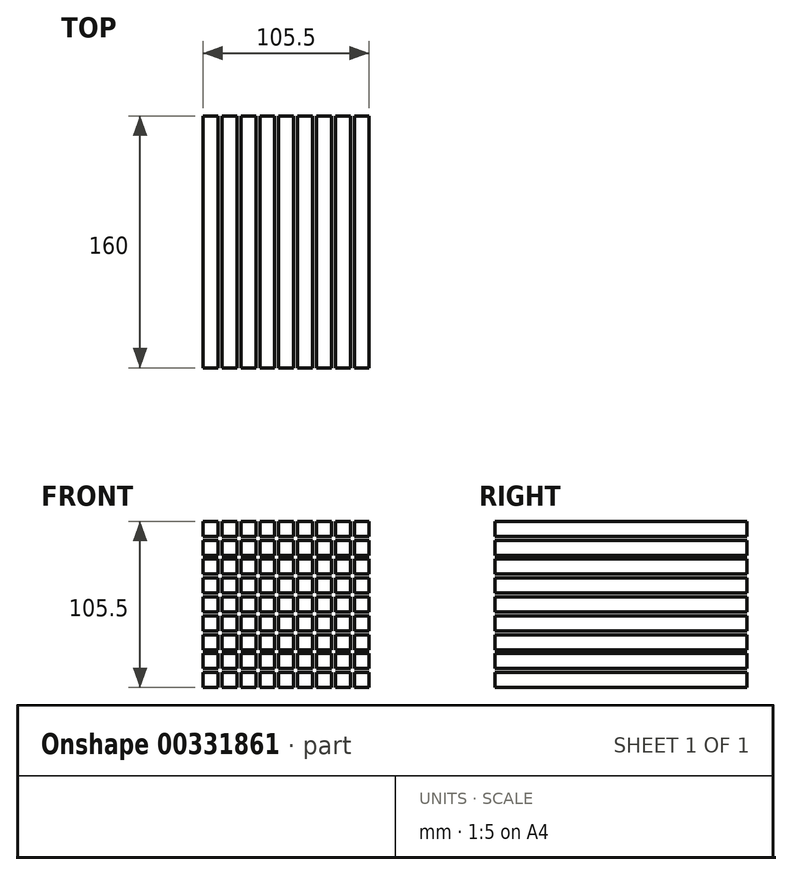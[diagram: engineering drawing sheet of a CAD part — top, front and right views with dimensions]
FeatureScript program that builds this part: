
annotation { "Feature Type Name" : "Feature", "Feature Type Description" : "" }
export const myFeature = defineFeature(function(context is Context, id is Id, definition is map)
    precondition{}
    {
        {
            var Q0;
            Q0=qCreatedBy(makeId("Front.planeOp"),FACE);
            var sketch = newSketch(context, id + "F0", { "sketchPlane" : qUnion([Q0])});
            skLineSegment(sketch, "E0.bottom", {"start": v(-46.46, 59.49) * mm, "end": v(-36.96, 59.49) * mm});
            skLineSegment(sketch, "E0.top", {"start": v(-46.46, 49.99) * mm, "end": v(-36.96, 49.99) * mm});
            skLineSegment(sketch, "E0.left", {"start": v(-46.46, 59.49) * mm, "end": v(-46.46, 49.99) * mm});
            skLineSegment(sketch, "E0.right", {"start": v(-36.96, 59.49) * mm, "end": v(-36.96, 49.99) * mm});
            skLineSegment(sketch, "E1.0.1.0", {"start": v(-46.46, 47.49) * mm, "end": v(-36.96, 47.49) * mm});
            skLineSegment(sketch, "E1.0.1.1", {"start": v(-46.46, 47.49) * mm, "end": v(-46.46, 37.99) * mm});
            skLineSegment(sketch, "E1.0.1.2", {"start": v(-46.46, 37.99) * mm, "end": v(-36.96, 37.99) * mm});
            skLineSegment(sketch, "E1.0.1.3", {"start": v(-36.96, 47.49) * mm, "end": v(-36.96, 37.99) * mm});
            skLineSegment(sketch, "E1.0.2.0", {"start": v(-46.46, 35.49) * mm, "end": v(-36.96, 35.49) * mm});
            skLineSegment(sketch, "E1.0.2.1", {"start": v(-46.46, 35.49) * mm, "end": v(-46.46, 25.99) * mm});
            skLineSegment(sketch, "E1.0.2.2", {"start": v(-46.46, 25.99) * mm, "end": v(-36.96, 25.99) * mm});
            skLineSegment(sketch, "E1.0.2.3", {"start": v(-36.96, 35.49) * mm, "end": v(-36.96, 25.99) * mm});
            skLineSegment(sketch, "E1.0.3.0", {"start": v(-46.46, 23.49) * mm, "end": v(-36.96, 23.49) * mm});
            skLineSegment(sketch, "E1.0.3.1", {"start": v(-46.46, 23.49) * mm, "end": v(-46.46, 13.99) * mm});
            skLineSegment(sketch, "E1.0.3.2", {"start": v(-46.46, 13.99) * mm, "end": v(-36.96, 13.99) * mm});
            skLineSegment(sketch, "E1.0.3.3", {"start": v(-36.96, 23.49) * mm, "end": v(-36.96, 13.99) * mm});
            skLineSegment(sketch, "E1.0.4.0", {"start": v(-46.46, 11.49) * mm, "end": v(-36.96, 11.49) * mm});
            skLineSegment(sketch, "E1.0.4.1", {"start": v(-46.46, 11.49) * mm, "end": v(-46.46, 1.99) * mm});
            skLineSegment(sketch, "E1.0.4.2", {"start": v(-46.46, 1.99) * mm, "end": v(-36.96, 1.99) * mm});
            skLineSegment(sketch, "E1.0.4.3", {"start": v(-36.96, 11.49) * mm, "end": v(-36.96, 1.99) * mm});
            skLineSegment(sketch, "E1.0.5.0", {"start": v(-46.46, -0.51) * mm, "end": v(-36.96, -0.51) * mm});
            skLineSegment(sketch, "E1.0.5.1", {"start": v(-46.46, -0.51) * mm, "end": v(-46.46, -10.01) * mm});
            skLineSegment(sketch, "E1.0.5.2", {"start": v(-46.46, -10.01) * mm, "end": v(-36.96, -10.01) * mm});
            skLineSegment(sketch, "E1.0.5.3", {"start": v(-36.96, -0.51) * mm, "end": v(-36.96, -10.01) * mm});
            skLineSegment(sketch, "E1.0.6.0", {"start": v(-46.46, -12.51) * mm, "end": v(-36.96, -12.51) * mm});
            skLineSegment(sketch, "E1.0.6.1", {"start": v(-46.46, -12.51) * mm, "end": v(-46.46, -22.01) * mm});
            skLineSegment(sketch, "E1.0.6.2", {"start": v(-46.46, -22.01) * mm, "end": v(-36.96, -22.01) * mm});
            skLineSegment(sketch, "E1.0.6.3", {"start": v(-36.96, -12.51) * mm, "end": v(-36.96, -22.01) * mm});
            skLineSegment(sketch, "E1.0.7.0", {"start": v(-46.46, -24.51) * mm, "end": v(-36.96, -24.51) * mm});
            skLineSegment(sketch, "E1.0.7.1", {"start": v(-46.46, -24.51) * mm, "end": v(-46.46, -34.01) * mm});
            skLineSegment(sketch, "E1.0.7.2", {"start": v(-46.46, -34.01) * mm, "end": v(-36.96, -34.01) * mm});
            skLineSegment(sketch, "E1.0.7.3", {"start": v(-36.96, -24.51) * mm, "end": v(-36.96, -34.01) * mm});
            skLineSegment(sketch, "E1.0.8.0", {"start": v(-46.46, -36.51) * mm, "end": v(-36.96, -36.51) * mm});
            skLineSegment(sketch, "E1.0.8.1", {"start": v(-46.46, -36.51) * mm, "end": v(-46.46, -46.01) * mm});
            skLineSegment(sketch, "E1.0.8.2", {"start": v(-46.46, -46.01) * mm, "end": v(-36.96, -46.01) * mm});
            skLineSegment(sketch, "E1.0.8.3", {"start": v(-36.96, -36.51) * mm, "end": v(-36.96, -46.01) * mm});
            skLineSegment(sketch, "E1.1.0.0", {"start": v(-34.46, 59.49) * mm, "end": v(-24.96, 59.49) * mm});
            skLineSegment(sketch, "E1.1.0.1", {"start": v(-34.46, 59.49) * mm, "end": v(-34.46, 49.99) * mm});
            skLineSegment(sketch, "E1.1.0.2", {"start": v(-34.46, 49.99) * mm, "end": v(-24.96, 49.99) * mm});
            skLineSegment(sketch, "E1.1.0.3", {"start": v(-24.96, 59.49) * mm, "end": v(-24.96, 49.99) * mm});
            skLineSegment(sketch, "E1.1.1.0", {"start": v(-34.46, 47.49) * mm, "end": v(-24.96, 47.49) * mm});
            skLineSegment(sketch, "E1.1.1.1", {"start": v(-34.46, 47.49) * mm, "end": v(-34.46, 37.99) * mm});
            skLineSegment(sketch, "E1.1.1.2", {"start": v(-34.46, 37.99) * mm, "end": v(-24.96, 37.99) * mm});
            skLineSegment(sketch, "E1.1.1.3", {"start": v(-24.96, 47.49) * mm, "end": v(-24.96, 37.99) * mm});
            skLineSegment(sketch, "E1.1.2.0", {"start": v(-34.46, 35.49) * mm, "end": v(-24.96, 35.49) * mm});
            skLineSegment(sketch, "E1.1.2.1", {"start": v(-34.46, 35.49) * mm, "end": v(-34.46, 25.99) * mm});
            skLineSegment(sketch, "E1.1.2.2", {"start": v(-34.46, 25.99) * mm, "end": v(-24.96, 25.99) * mm});
            skLineSegment(sketch, "E1.1.2.3", {"start": v(-24.96, 35.49) * mm, "end": v(-24.96, 25.99) * mm});
            skLineSegment(sketch, "E1.1.3.0", {"start": v(-34.46, 23.49) * mm, "end": v(-24.96, 23.49) * mm});
            skLineSegment(sketch, "E1.1.3.1", {"start": v(-34.46, 23.49) * mm, "end": v(-34.46, 13.99) * mm});
            skLineSegment(sketch, "E1.1.3.2", {"start": v(-34.46, 13.99) * mm, "end": v(-24.96, 13.99) * mm});
            skLineSegment(sketch, "E1.1.3.3", {"start": v(-24.96, 23.49) * mm, "end": v(-24.96, 13.99) * mm});
            skLineSegment(sketch, "E1.1.4.0", {"start": v(-34.46, 11.49) * mm, "end": v(-24.96, 11.49) * mm});
            skLineSegment(sketch, "E1.1.4.1", {"start": v(-34.46, 11.49) * mm, "end": v(-34.46, 1.99) * mm});
            skLineSegment(sketch, "E1.1.4.2", {"start": v(-34.46, 1.99) * mm, "end": v(-24.96, 1.99) * mm});
            skLineSegment(sketch, "E1.1.4.3", {"start": v(-24.96, 11.49) * mm, "end": v(-24.96, 1.99) * mm});
            skLineSegment(sketch, "E1.1.5.0", {"start": v(-34.46, -0.51) * mm, "end": v(-24.96, -0.51) * mm});
            skLineSegment(sketch, "E1.1.5.1", {"start": v(-34.46, -0.51) * mm, "end": v(-34.46, -10.01) * mm});
            skLineSegment(sketch, "E1.1.5.2", {"start": v(-34.46, -10.01) * mm, "end": v(-24.96, -10.01) * mm});
            skLineSegment(sketch, "E1.1.5.3", {"start": v(-24.96, -0.51) * mm, "end": v(-24.96, -10.01) * mm});
            skLineSegment(sketch, "E1.1.6.0", {"start": v(-34.46, -12.51) * mm, "end": v(-24.96, -12.51) * mm});
            skLineSegment(sketch, "E1.1.6.1", {"start": v(-34.46, -12.51) * mm, "end": v(-34.46, -22.01) * mm});
            skLineSegment(sketch, "E1.1.6.2", {"start": v(-34.46, -22.01) * mm, "end": v(-24.96, -22.01) * mm});
            skLineSegment(sketch, "E1.1.6.3", {"start": v(-24.96, -12.51) * mm, "end": v(-24.96, -22.01) * mm});
            skLineSegment(sketch, "E1.1.7.0", {"start": v(-34.46, -24.51) * mm, "end": v(-24.96, -24.51) * mm});
            skLineSegment(sketch, "E1.1.7.1", {"start": v(-34.46, -24.51) * mm, "end": v(-34.46, -34.01) * mm});
            skLineSegment(sketch, "E1.1.7.2", {"start": v(-34.46, -34.01) * mm, "end": v(-24.96, -34.01) * mm});
            skLineSegment(sketch, "E1.1.7.3", {"start": v(-24.96, -24.51) * mm, "end": v(-24.96, -34.01) * mm});
            skLineSegment(sketch, "E1.1.8.0", {"start": v(-34.46, -36.51) * mm, "end": v(-24.96, -36.51) * mm});
            skLineSegment(sketch, "E1.1.8.1", {"start": v(-34.46, -36.51) * mm, "end": v(-34.46, -46.01) * mm});
            skLineSegment(sketch, "E1.1.8.2", {"start": v(-34.46, -46.01) * mm, "end": v(-24.96, -46.01) * mm});
            skLineSegment(sketch, "E1.1.8.3", {"start": v(-24.96, -36.51) * mm, "end": v(-24.96, -46.01) * mm});
            skLineSegment(sketch, "E1.2.0.0", {"start": v(-22.46, 59.49) * mm, "end": v(-12.96, 59.49) * mm});
            skLineSegment(sketch, "E1.2.0.1", {"start": v(-22.46, 59.49) * mm, "end": v(-22.46, 49.99) * mm});
            skLineSegment(sketch, "E1.2.0.2", {"start": v(-22.46, 49.99) * mm, "end": v(-12.96, 49.99) * mm});
            skLineSegment(sketch, "E1.2.0.3", {"start": v(-12.96, 59.49) * mm, "end": v(-12.96, 49.99) * mm});
            skLineSegment(sketch, "E1.2.1.0", {"start": v(-22.46, 47.49) * mm, "end": v(-12.96, 47.49) * mm});
            skLineSegment(sketch, "E1.2.1.1", {"start": v(-22.46, 47.49) * mm, "end": v(-22.46, 37.99) * mm});
            skLineSegment(sketch, "E1.2.1.2", {"start": v(-22.46, 37.99) * mm, "end": v(-12.96, 37.99) * mm});
            skLineSegment(sketch, "E1.2.1.3", {"start": v(-12.96, 47.49) * mm, "end": v(-12.96, 37.99) * mm});
            skLineSegment(sketch, "E1.2.2.0", {"start": v(-22.46, 35.49) * mm, "end": v(-12.96, 35.49) * mm});
            skLineSegment(sketch, "E1.2.2.1", {"start": v(-22.46, 35.49) * mm, "end": v(-22.46, 25.99) * mm});
            skLineSegment(sketch, "E1.2.2.2", {"start": v(-22.46, 25.99) * mm, "end": v(-12.96, 25.99) * mm});
            skLineSegment(sketch, "E1.2.2.3", {"start": v(-12.96, 35.49) * mm, "end": v(-12.96, 25.99) * mm});
            skLineSegment(sketch, "E1.2.3.0", {"start": v(-22.46, 23.49) * mm, "end": v(-12.96, 23.49) * mm});
            skLineSegment(sketch, "E1.2.3.1", {"start": v(-22.46, 23.49) * mm, "end": v(-22.46, 13.99) * mm});
            skLineSegment(sketch, "E1.2.3.2", {"start": v(-22.46, 13.99) * mm, "end": v(-12.96, 13.99) * mm});
            skLineSegment(sketch, "E1.2.3.3", {"start": v(-12.96, 23.49) * mm, "end": v(-12.96, 13.99) * mm});
            skLineSegment(sketch, "E1.2.4.0", {"start": v(-22.46, 11.49) * mm, "end": v(-12.96, 11.49) * mm});
            skLineSegment(sketch, "E1.2.4.1", {"start": v(-22.46, 11.49) * mm, "end": v(-22.46, 1.99) * mm});
            skLineSegment(sketch, "E1.2.4.2", {"start": v(-22.46, 1.99) * mm, "end": v(-12.96, 1.99) * mm});
            skLineSegment(sketch, "E1.2.4.3", {"start": v(-12.96, 11.49) * mm, "end": v(-12.96, 1.99) * mm});
            skLineSegment(sketch, "E1.2.5.0", {"start": v(-22.46, -0.51) * mm, "end": v(-12.96, -0.51) * mm});
            skLineSegment(sketch, "E1.2.5.1", {"start": v(-22.46, -0.51) * mm, "end": v(-22.46, -10.01) * mm});
            skLineSegment(sketch, "E1.2.5.2", {"start": v(-22.46, -10.01) * mm, "end": v(-12.96, -10.01) * mm});
            skLineSegment(sketch, "E1.2.5.3", {"start": v(-12.96, -0.51) * mm, "end": v(-12.96, -10.01) * mm});
            skLineSegment(sketch, "E1.2.6.0", {"start": v(-22.46, -12.51) * mm, "end": v(-12.96, -12.51) * mm});
            skLineSegment(sketch, "E1.2.6.1", {"start": v(-22.46, -12.51) * mm, "end": v(-22.46, -22.01) * mm});
            skLineSegment(sketch, "E1.2.6.2", {"start": v(-22.46, -22.01) * mm, "end": v(-12.96, -22.01) * mm});
            skLineSegment(sketch, "E1.2.6.3", {"start": v(-12.96, -12.51) * mm, "end": v(-12.96, -22.01) * mm});
            skLineSegment(sketch, "E1.2.7.0", {"start": v(-22.46, -24.51) * mm, "end": v(-12.96, -24.51) * mm});
            skLineSegment(sketch, "E1.2.7.1", {"start": v(-22.46, -24.51) * mm, "end": v(-22.46, -34.01) * mm});
            skLineSegment(sketch, "E1.2.7.2", {"start": v(-22.46, -34.01) * mm, "end": v(-12.96, -34.01) * mm});
            skLineSegment(sketch, "E1.2.7.3", {"start": v(-12.96, -24.51) * mm, "end": v(-12.96, -34.01) * mm});
            skLineSegment(sketch, "E1.2.8.0", {"start": v(-22.46, -36.51) * mm, "end": v(-12.96, -36.51) * mm});
            skLineSegment(sketch, "E1.2.8.1", {"start": v(-22.46, -36.51) * mm, "end": v(-22.46, -46.01) * mm});
            skLineSegment(sketch, "E1.2.8.2", {"start": v(-22.46, -46.01) * mm, "end": v(-12.96, -46.01) * mm});
            skLineSegment(sketch, "E1.2.8.3", {"start": v(-12.96, -36.51) * mm, "end": v(-12.96, -46.01) * mm});
            skLineSegment(sketch, "E1.3.0.0", {"start": v(-10.46, 59.49) * mm, "end": v(-0.96, 59.49) * mm});
            skLineSegment(sketch, "E1.3.0.1", {"start": v(-10.46, 59.49) * mm, "end": v(-10.46, 49.99) * mm});
            skLineSegment(sketch, "E1.3.0.2", {"start": v(-10.46, 49.99) * mm, "end": v(-0.96, 49.99) * mm});
            skLineSegment(sketch, "E1.3.0.3", {"start": v(-0.96, 59.49) * mm, "end": v(-0.96, 49.99) * mm});
            skLineSegment(sketch, "E1.3.1.0", {"start": v(-10.46, 47.49) * mm, "end": v(-0.96, 47.49) * mm});
            skLineSegment(sketch, "E1.3.1.1", {"start": v(-10.46, 47.49) * mm, "end": v(-10.46, 37.99) * mm});
            skLineSegment(sketch, "E1.3.1.2", {"start": v(-10.46, 37.99) * mm, "end": v(-0.96, 37.99) * mm});
            skLineSegment(sketch, "E1.3.1.3", {"start": v(-0.96, 47.49) * mm, "end": v(-0.96, 37.99) * mm});
            skLineSegment(sketch, "E1.3.2.0", {"start": v(-10.46, 35.49) * mm, "end": v(-0.96, 35.49) * mm});
            skLineSegment(sketch, "E1.3.2.1", {"start": v(-10.46, 35.49) * mm, "end": v(-10.46, 25.99) * mm});
            skLineSegment(sketch, "E1.3.2.2", {"start": v(-10.46, 25.99) * mm, "end": v(-0.96, 25.99) * mm});
            skLineSegment(sketch, "E1.3.2.3", {"start": v(-0.96, 35.49) * mm, "end": v(-0.96, 25.99) * mm});
            skLineSegment(sketch, "E1.3.3.0", {"start": v(-10.46, 23.49) * mm, "end": v(-0.96, 23.49) * mm});
            skLineSegment(sketch, "E1.3.3.1", {"start": v(-10.46, 23.49) * mm, "end": v(-10.46, 13.99) * mm});
            skLineSegment(sketch, "E1.3.3.2", {"start": v(-10.46, 13.99) * mm, "end": v(-0.96, 13.99) * mm});
            skLineSegment(sketch, "E1.3.3.3", {"start": v(-0.96, 23.49) * mm, "end": v(-0.96, 13.99) * mm});
            skLineSegment(sketch, "E1.3.4.0", {"start": v(-10.46, 11.49) * mm, "end": v(-0.96, 11.49) * mm});
            skLineSegment(sketch, "E1.3.4.1", {"start": v(-10.46, 11.49) * mm, "end": v(-10.46, 1.99) * mm});
            skLineSegment(sketch, "E1.3.4.2", {"start": v(-10.46, 1.99) * mm, "end": v(-0.96, 1.99) * mm});
            skLineSegment(sketch, "E1.3.4.3", {"start": v(-0.96, 11.49) * mm, "end": v(-0.96, 1.99) * mm});
            skLineSegment(sketch, "E1.3.5.0", {"start": v(-10.46, -0.51) * mm, "end": v(-0.96, -0.51) * mm});
            skLineSegment(sketch, "E1.3.5.1", {"start": v(-10.46, -0.51) * mm, "end": v(-10.46, -10.01) * mm});
            skLineSegment(sketch, "E1.3.5.2", {"start": v(-10.46, -10.01) * mm, "end": v(-0.96, -10.01) * mm});
            skLineSegment(sketch, "E1.3.5.3", {"start": v(-0.96, -0.51) * mm, "end": v(-0.96, -10.01) * mm});
            skLineSegment(sketch, "E1.3.6.0", {"start": v(-10.46, -12.51) * mm, "end": v(-0.96, -12.51) * mm});
            skLineSegment(sketch, "E1.3.6.1", {"start": v(-10.46, -12.51) * mm, "end": v(-10.46, -22.01) * mm});
            skLineSegment(sketch, "E1.3.6.2", {"start": v(-10.46, -22.01) * mm, "end": v(-0.96, -22.01) * mm});
            skLineSegment(sketch, "E1.3.6.3", {"start": v(-0.96, -12.51) * mm, "end": v(-0.96, -22.01) * mm});
            skLineSegment(sketch, "E1.3.7.0", {"start": v(-10.46, -24.51) * mm, "end": v(-0.96, -24.51) * mm});
            skLineSegment(sketch, "E1.3.7.1", {"start": v(-10.46, -24.51) * mm, "end": v(-10.46, -34.01) * mm});
            skLineSegment(sketch, "E1.3.7.2", {"start": v(-10.46, -34.01) * mm, "end": v(-0.96, -34.01) * mm});
            skLineSegment(sketch, "E1.3.7.3", {"start": v(-0.96, -24.51) * mm, "end": v(-0.96, -34.01) * mm});
            skLineSegment(sketch, "E1.3.8.0", {"start": v(-10.46, -36.51) * mm, "end": v(-0.96, -36.51) * mm});
            skLineSegment(sketch, "E1.3.8.1", {"start": v(-10.46, -36.51) * mm, "end": v(-10.46, -46.01) * mm});
            skLineSegment(sketch, "E1.3.8.2", {"start": v(-10.46, -46.01) * mm, "end": v(-0.96, -46.01) * mm});
            skLineSegment(sketch, "E1.3.8.3", {"start": v(-0.96, -36.51) * mm, "end": v(-0.96, -46.01) * mm});
            skLineSegment(sketch, "E1.4.0.0", {"start": v(1.54, 59.49) * mm, "end": v(11.04, 59.49) * mm});
            skLineSegment(sketch, "E1.4.0.1", {"start": v(1.54, 59.49) * mm, "end": v(1.54, 49.99) * mm});
            skLineSegment(sketch, "E1.4.0.2", {"start": v(1.54, 49.99) * mm, "end": v(11.04, 49.99) * mm});
            skLineSegment(sketch, "E1.4.0.3", {"start": v(11.04, 59.49) * mm, "end": v(11.04, 49.99) * mm});
            skLineSegment(sketch, "E1.4.1.0", {"start": v(1.54, 47.49) * mm, "end": v(11.04, 47.49) * mm});
            skLineSegment(sketch, "E1.4.1.1", {"start": v(1.54, 47.49) * mm, "end": v(1.54, 37.99) * mm});
            skLineSegment(sketch, "E1.4.1.2", {"start": v(1.54, 37.99) * mm, "end": v(11.04, 37.99) * mm});
            skLineSegment(sketch, "E1.4.1.3", {"start": v(11.04, 47.49) * mm, "end": v(11.04, 37.99) * mm});
            skLineSegment(sketch, "E1.4.2.0", {"start": v(1.54, 35.49) * mm, "end": v(11.04, 35.49) * mm});
            skLineSegment(sketch, "E1.4.2.1", {"start": v(1.54, 35.49) * mm, "end": v(1.54, 25.99) * mm});
            skLineSegment(sketch, "E1.4.2.2", {"start": v(1.54, 25.99) * mm, "end": v(11.04, 25.99) * mm});
            skLineSegment(sketch, "E1.4.2.3", {"start": v(11.04, 35.49) * mm, "end": v(11.04, 25.99) * mm});
            skLineSegment(sketch, "E1.4.3.0", {"start": v(1.54, 23.49) * mm, "end": v(11.04, 23.49) * mm});
            skLineSegment(sketch, "E1.4.3.1", {"start": v(1.54, 23.49) * mm, "end": v(1.54, 13.99) * mm});
            skLineSegment(sketch, "E1.4.3.2", {"start": v(1.54, 13.99) * mm, "end": v(11.04, 13.99) * mm});
            skLineSegment(sketch, "E1.4.3.3", {"start": v(11.04, 23.49) * mm, "end": v(11.04, 13.99) * mm});
            skLineSegment(sketch, "E1.4.4.0", {"start": v(1.54, 11.49) * mm, "end": v(11.04, 11.49) * mm});
            skLineSegment(sketch, "E1.4.4.1", {"start": v(1.54, 11.49) * mm, "end": v(1.54, 1.99) * mm});
            skLineSegment(sketch, "E1.4.4.2", {"start": v(1.54, 1.99) * mm, "end": v(11.04, 1.99) * mm});
            skLineSegment(sketch, "E1.4.4.3", {"start": v(11.04, 11.49) * mm, "end": v(11.04, 1.99) * mm});
            skLineSegment(sketch, "E1.4.5.0", {"start": v(1.54, -0.51) * mm, "end": v(11.04, -0.51) * mm});
            skLineSegment(sketch, "E1.4.5.1", {"start": v(1.54, -0.51) * mm, "end": v(1.54, -10.01) * mm});
            skLineSegment(sketch, "E1.4.5.2", {"start": v(1.54, -10.01) * mm, "end": v(11.04, -10.01) * mm});
            skLineSegment(sketch, "E1.4.5.3", {"start": v(11.04, -0.51) * mm, "end": v(11.04, -10.01) * mm});
            skLineSegment(sketch, "E1.4.6.0", {"start": v(1.54, -12.51) * mm, "end": v(11.04, -12.51) * mm});
            skLineSegment(sketch, "E1.4.6.1", {"start": v(1.54, -12.51) * mm, "end": v(1.54, -22.01) * mm});
            skLineSegment(sketch, "E1.4.6.2", {"start": v(1.54, -22.01) * mm, "end": v(11.04, -22.01) * mm});
            skLineSegment(sketch, "E1.4.6.3", {"start": v(11.04, -12.51) * mm, "end": v(11.04, -22.01) * mm});
            skLineSegment(sketch, "E1.4.7.0", {"start": v(1.54, -24.51) * mm, "end": v(11.04, -24.51) * mm});
            skLineSegment(sketch, "E1.4.7.1", {"start": v(1.54, -24.51) * mm, "end": v(1.54, -34.01) * mm});
            skLineSegment(sketch, "E1.4.7.2", {"start": v(1.54, -34.01) * mm, "end": v(11.04, -34.01) * mm});
            skLineSegment(sketch, "E1.4.7.3", {"start": v(11.04, -24.51) * mm, "end": v(11.04, -34.01) * mm});
            skLineSegment(sketch, "E1.4.8.0", {"start": v(1.54, -36.51) * mm, "end": v(11.04, -36.51) * mm});
            skLineSegment(sketch, "E1.4.8.1", {"start": v(1.54, -36.51) * mm, "end": v(1.54, -46.01) * mm});
            skLineSegment(sketch, "E1.4.8.2", {"start": v(1.54, -46.01) * mm, "end": v(11.04, -46.01) * mm});
            skLineSegment(sketch, "E1.4.8.3", {"start": v(11.04, -36.51) * mm, "end": v(11.04, -46.01) * mm});
            skLineSegment(sketch, "E1.5.0.0", {"start": v(13.54, 59.49) * mm, "end": v(23.04, 59.49) * mm});
            skLineSegment(sketch, "E1.5.0.1", {"start": v(13.54, 59.49) * mm, "end": v(13.54, 49.99) * mm});
            skLineSegment(sketch, "E1.5.0.2", {"start": v(13.54, 49.99) * mm, "end": v(23.04, 49.99) * mm});
            skLineSegment(sketch, "E1.5.0.3", {"start": v(23.04, 59.49) * mm, "end": v(23.04, 49.99) * mm});
            skLineSegment(sketch, "E1.5.1.0", {"start": v(13.54, 47.49) * mm, "end": v(23.04, 47.49) * mm});
            skLineSegment(sketch, "E1.5.1.1", {"start": v(13.54, 47.49) * mm, "end": v(13.54, 37.99) * mm});
            skLineSegment(sketch, "E1.5.1.2", {"start": v(13.54, 37.99) * mm, "end": v(23.04, 37.99) * mm});
            skLineSegment(sketch, "E1.5.1.3", {"start": v(23.04, 47.49) * mm, "end": v(23.04, 37.99) * mm});
            skLineSegment(sketch, "E1.5.2.0", {"start": v(13.54, 35.49) * mm, "end": v(23.04, 35.49) * mm});
            skLineSegment(sketch, "E1.5.2.1", {"start": v(13.54, 35.49) * mm, "end": v(13.54, 25.99) * mm});
            skLineSegment(sketch, "E1.5.2.2", {"start": v(13.54, 25.99) * mm, "end": v(23.04, 25.99) * mm});
            skLineSegment(sketch, "E1.5.2.3", {"start": v(23.04, 35.49) * mm, "end": v(23.04, 25.99) * mm});
            skLineSegment(sketch, "E1.5.3.0", {"start": v(13.54, 23.49) * mm, "end": v(23.04, 23.49) * mm});
            skLineSegment(sketch, "E1.5.3.1", {"start": v(13.54, 23.49) * mm, "end": v(13.54, 13.99) * mm});
            skLineSegment(sketch, "E1.5.3.2", {"start": v(13.54, 13.99) * mm, "end": v(23.04, 13.99) * mm});
            skLineSegment(sketch, "E1.5.3.3", {"start": v(23.04, 23.49) * mm, "end": v(23.04, 13.99) * mm});
            skLineSegment(sketch, "E1.5.4.0", {"start": v(13.54, 11.49) * mm, "end": v(23.04, 11.49) * mm});
            skLineSegment(sketch, "E1.5.4.1", {"start": v(13.54, 11.49) * mm, "end": v(13.54, 1.99) * mm});
            skLineSegment(sketch, "E1.5.4.2", {"start": v(13.54, 1.99) * mm, "end": v(23.04, 1.99) * mm});
            skLineSegment(sketch, "E1.5.4.3", {"start": v(23.04, 11.49) * mm, "end": v(23.04, 1.99) * mm});
            skLineSegment(sketch, "E1.5.5.0", {"start": v(13.54, -0.51) * mm, "end": v(23.04, -0.51) * mm});
            skLineSegment(sketch, "E1.5.5.1", {"start": v(13.54, -0.51) * mm, "end": v(13.54, -10.01) * mm});
            skLineSegment(sketch, "E1.5.5.2", {"start": v(13.54, -10.01) * mm, "end": v(23.04, -10.01) * mm});
            skLineSegment(sketch, "E1.5.5.3", {"start": v(23.04, -0.51) * mm, "end": v(23.04, -10.01) * mm});
            skLineSegment(sketch, "E1.5.6.0", {"start": v(13.54, -12.51) * mm, "end": v(23.04, -12.51) * mm});
            skLineSegment(sketch, "E1.5.6.1", {"start": v(13.54, -12.51) * mm, "end": v(13.54, -22.01) * mm});
            skLineSegment(sketch, "E1.5.6.2", {"start": v(13.54, -22.01) * mm, "end": v(23.04, -22.01) * mm});
            skLineSegment(sketch, "E1.5.6.3", {"start": v(23.04, -12.51) * mm, "end": v(23.04, -22.01) * mm});
            skLineSegment(sketch, "E1.5.7.0", {"start": v(13.54, -24.51) * mm, "end": v(23.04, -24.51) * mm});
            skLineSegment(sketch, "E1.5.7.1", {"start": v(13.54, -24.51) * mm, "end": v(13.54, -34.01) * mm});
            skLineSegment(sketch, "E1.5.7.2", {"start": v(13.54, -34.01) * mm, "end": v(23.04, -34.01) * mm});
            skLineSegment(sketch, "E1.5.7.3", {"start": v(23.04, -24.51) * mm, "end": v(23.04, -34.01) * mm});
            skLineSegment(sketch, "E1.5.8.0", {"start": v(13.54, -36.51) * mm, "end": v(23.04, -36.51) * mm});
            skLineSegment(sketch, "E1.5.8.1", {"start": v(13.54, -36.51) * mm, "end": v(13.54, -46.01) * mm});
            skLineSegment(sketch, "E1.5.8.2", {"start": v(13.54, -46.01) * mm, "end": v(23.04, -46.01) * mm});
            skLineSegment(sketch, "E1.5.8.3", {"start": v(23.04, -36.51) * mm, "end": v(23.04, -46.01) * mm});
            skLineSegment(sketch, "E1.6.0.0", {"start": v(25.54, 59.49) * mm, "end": v(35.04, 59.49) * mm});
            skLineSegment(sketch, "E1.6.0.1", {"start": v(25.54, 59.49) * mm, "end": v(25.54, 49.99) * mm});
            skLineSegment(sketch, "E1.6.0.2", {"start": v(25.54, 49.99) * mm, "end": v(35.04, 49.99) * mm});
            skLineSegment(sketch, "E1.6.0.3", {"start": v(35.04, 59.49) * mm, "end": v(35.04, 49.99) * mm});
            skLineSegment(sketch, "E1.6.1.0", {"start": v(25.54, 47.49) * mm, "end": v(35.04, 47.49) * mm});
            skLineSegment(sketch, "E1.6.1.1", {"start": v(25.54, 47.49) * mm, "end": v(25.54, 37.99) * mm});
            skLineSegment(sketch, "E1.6.1.2", {"start": v(25.54, 37.99) * mm, "end": v(35.04, 37.99) * mm});
            skLineSegment(sketch, "E1.6.1.3", {"start": v(35.04, 47.49) * mm, "end": v(35.04, 37.99) * mm});
            skLineSegment(sketch, "E1.6.2.0", {"start": v(25.54, 35.49) * mm, "end": v(35.04, 35.49) * mm});
            skLineSegment(sketch, "E1.6.2.1", {"start": v(25.54, 35.49) * mm, "end": v(25.54, 25.99) * mm});
            skLineSegment(sketch, "E1.6.2.2", {"start": v(25.54, 25.99) * mm, "end": v(35.04, 25.99) * mm});
            skLineSegment(sketch, "E1.6.2.3", {"start": v(35.04, 35.49) * mm, "end": v(35.04, 25.99) * mm});
            skLineSegment(sketch, "E1.6.3.0", {"start": v(25.54, 23.49) * mm, "end": v(35.04, 23.49) * mm});
            skLineSegment(sketch, "E1.6.3.1", {"start": v(25.54, 23.49) * mm, "end": v(25.54, 13.99) * mm});
            skLineSegment(sketch, "E1.6.3.2", {"start": v(25.54, 13.99) * mm, "end": v(35.04, 13.99) * mm});
            skLineSegment(sketch, "E1.6.3.3", {"start": v(35.04, 23.49) * mm, "end": v(35.04, 13.99) * mm});
            skLineSegment(sketch, "E1.6.4.0", {"start": v(25.54, 11.49) * mm, "end": v(35.04, 11.49) * mm});
            skLineSegment(sketch, "E1.6.4.1", {"start": v(25.54, 11.49) * mm, "end": v(25.54, 1.99) * mm});
            skLineSegment(sketch, "E1.6.4.2", {"start": v(25.54, 1.99) * mm, "end": v(35.04, 1.99) * mm});
            skLineSegment(sketch, "E1.6.4.3", {"start": v(35.04, 11.49) * mm, "end": v(35.04, 1.99) * mm});
            skLineSegment(sketch, "E1.6.5.0", {"start": v(25.54, -0.51) * mm, "end": v(35.04, -0.51) * mm});
            skLineSegment(sketch, "E1.6.5.1", {"start": v(25.54, -0.51) * mm, "end": v(25.54, -10.01) * mm});
            skLineSegment(sketch, "E1.6.5.2", {"start": v(25.54, -10.01) * mm, "end": v(35.04, -10.01) * mm});
            skLineSegment(sketch, "E1.6.5.3", {"start": v(35.04, -0.51) * mm, "end": v(35.04, -10.01) * mm});
            skLineSegment(sketch, "E1.6.6.0", {"start": v(25.54, -12.51) * mm, "end": v(35.04, -12.51) * mm});
            skLineSegment(sketch, "E1.6.6.1", {"start": v(25.54, -12.51) * mm, "end": v(25.54, -22.01) * mm});
            skLineSegment(sketch, "E1.6.6.2", {"start": v(25.54, -22.01) * mm, "end": v(35.04, -22.01) * mm});
            skLineSegment(sketch, "E1.6.6.3", {"start": v(35.04, -12.51) * mm, "end": v(35.04, -22.01) * mm});
            skLineSegment(sketch, "E1.6.7.0", {"start": v(25.54, -24.51) * mm, "end": v(35.04, -24.51) * mm});
            skLineSegment(sketch, "E1.6.7.1", {"start": v(25.54, -24.51) * mm, "end": v(25.54, -34.01) * mm});
            skLineSegment(sketch, "E1.6.7.2", {"start": v(25.54, -34.01) * mm, "end": v(35.04, -34.01) * mm});
            skLineSegment(sketch, "E1.6.7.3", {"start": v(35.04, -24.51) * mm, "end": v(35.04, -34.01) * mm});
            skLineSegment(sketch, "E1.6.8.0", {"start": v(25.54, -36.51) * mm, "end": v(35.04, -36.51) * mm});
            skLineSegment(sketch, "E1.6.8.1", {"start": v(25.54, -36.51) * mm, "end": v(25.54, -46.01) * mm});
            skLineSegment(sketch, "E1.6.8.2", {"start": v(25.54, -46.01) * mm, "end": v(35.04, -46.01) * mm});
            skLineSegment(sketch, "E1.6.8.3", {"start": v(35.04, -36.51) * mm, "end": v(35.04, -46.01) * mm});
            skLineSegment(sketch, "E1.7.0.0", {"start": v(37.54, 59.49) * mm, "end": v(47.04, 59.49) * mm});
            skLineSegment(sketch, "E1.7.0.1", {"start": v(37.54, 59.49) * mm, "end": v(37.54, 49.99) * mm});
            skLineSegment(sketch, "E1.7.0.2", {"start": v(37.54, 49.99) * mm, "end": v(47.04, 49.99) * mm});
            skLineSegment(sketch, "E1.7.0.3", {"start": v(47.04, 59.49) * mm, "end": v(47.04, 49.99) * mm});
            skLineSegment(sketch, "E1.7.1.0", {"start": v(37.54, 47.49) * mm, "end": v(47.04, 47.49) * mm});
            skLineSegment(sketch, "E1.7.1.1", {"start": v(37.54, 47.49) * mm, "end": v(37.54, 37.99) * mm});
            skLineSegment(sketch, "E1.7.1.2", {"start": v(37.54, 37.99) * mm, "end": v(47.04, 37.99) * mm});
            skLineSegment(sketch, "E1.7.1.3", {"start": v(47.04, 47.49) * mm, "end": v(47.04, 37.99) * mm});
            skLineSegment(sketch, "E1.7.2.0", {"start": v(37.54, 35.49) * mm, "end": v(47.04, 35.49) * mm});
            skLineSegment(sketch, "E1.7.2.1", {"start": v(37.54, 35.49) * mm, "end": v(37.54, 25.99) * mm});
            skLineSegment(sketch, "E1.7.2.2", {"start": v(37.54, 25.99) * mm, "end": v(47.04, 25.99) * mm});
            skLineSegment(sketch, "E1.7.2.3", {"start": v(47.04, 35.49) * mm, "end": v(47.04, 25.99) * mm});
            skLineSegment(sketch, "E1.7.3.0", {"start": v(37.54, 23.49) * mm, "end": v(47.04, 23.49) * mm});
            skLineSegment(sketch, "E1.7.3.1", {"start": v(37.54, 23.49) * mm, "end": v(37.54, 13.99) * mm});
            skLineSegment(sketch, "E1.7.3.2", {"start": v(37.54, 13.99) * mm, "end": v(47.04, 13.99) * mm});
            skLineSegment(sketch, "E1.7.3.3", {"start": v(47.04, 23.49) * mm, "end": v(47.04, 13.99) * mm});
            skLineSegment(sketch, "E1.7.4.0", {"start": v(37.54, 11.49) * mm, "end": v(47.04, 11.49) * mm});
            skLineSegment(sketch, "E1.7.4.1", {"start": v(37.54, 11.49) * mm, "end": v(37.54, 1.99) * mm});
            skLineSegment(sketch, "E1.7.4.2", {"start": v(37.54, 1.99) * mm, "end": v(47.04, 1.99) * mm});
            skLineSegment(sketch, "E1.7.4.3", {"start": v(47.04, 11.49) * mm, "end": v(47.04, 1.99) * mm});
            skLineSegment(sketch, "E1.7.5.0", {"start": v(37.54, -0.51) * mm, "end": v(47.04, -0.51) * mm});
            skLineSegment(sketch, "E1.7.5.1", {"start": v(37.54, -0.51) * mm, "end": v(37.54, -10.01) * mm});
            skLineSegment(sketch, "E1.7.5.2", {"start": v(37.54, -10.01) * mm, "end": v(47.04, -10.01) * mm});
            skLineSegment(sketch, "E1.7.5.3", {"start": v(47.04, -0.51) * mm, "end": v(47.04, -10.01) * mm});
            skLineSegment(sketch, "E1.7.6.0", {"start": v(37.54, -12.51) * mm, "end": v(47.04, -12.51) * mm});
            skLineSegment(sketch, "E1.7.6.1", {"start": v(37.54, -12.51) * mm, "end": v(37.54, -22.01) * mm});
            skLineSegment(sketch, "E1.7.6.2", {"start": v(37.54, -22.01) * mm, "end": v(47.04, -22.01) * mm});
            skLineSegment(sketch, "E1.7.6.3", {"start": v(47.04, -12.51) * mm, "end": v(47.04, -22.01) * mm});
            skLineSegment(sketch, "E1.7.7.0", {"start": v(37.54, -24.51) * mm, "end": v(47.04, -24.51) * mm});
            skLineSegment(sketch, "E1.7.7.1", {"start": v(37.54, -24.51) * mm, "end": v(37.54, -34.01) * mm});
            skLineSegment(sketch, "E1.7.7.2", {"start": v(37.54, -34.01) * mm, "end": v(47.04, -34.01) * mm});
            skLineSegment(sketch, "E1.7.7.3", {"start": v(47.04, -24.51) * mm, "end": v(47.04, -34.01) * mm});
            skLineSegment(sketch, "E1.7.8.0", {"start": v(37.54, -36.51) * mm, "end": v(47.04, -36.51) * mm});
            skLineSegment(sketch, "E1.7.8.1", {"start": v(37.54, -36.51) * mm, "end": v(37.54, -46.01) * mm});
            skLineSegment(sketch, "E1.7.8.2", {"start": v(37.54, -46.01) * mm, "end": v(47.04, -46.01) * mm});
            skLineSegment(sketch, "E1.7.8.3", {"start": v(47.04, -36.51) * mm, "end": v(47.04, -46.01) * mm});
            skLineSegment(sketch, "E1.8.0.0", {"start": v(49.54, 59.49) * mm, "end": v(59.04, 59.49) * mm});
            skLineSegment(sketch, "E1.8.0.1", {"start": v(49.54, 59.49) * mm, "end": v(49.54, 49.99) * mm});
            skLineSegment(sketch, "E1.8.0.2", {"start": v(49.54, 49.99) * mm, "end": v(59.04, 49.99) * mm});
            skLineSegment(sketch, "E1.8.0.3", {"start": v(59.04, 59.49) * mm, "end": v(59.04, 49.99) * mm});
            skLineSegment(sketch, "E1.8.1.0", {"start": v(49.54, 47.49) * mm, "end": v(59.04, 47.49) * mm});
            skLineSegment(sketch, "E1.8.1.1", {"start": v(49.54, 47.49) * mm, "end": v(49.54, 37.99) * mm});
            skLineSegment(sketch, "E1.8.1.2", {"start": v(49.54, 37.99) * mm, "end": v(59.04, 37.99) * mm});
            skLineSegment(sketch, "E1.8.1.3", {"start": v(59.04, 47.49) * mm, "end": v(59.04, 37.99) * mm});
            skLineSegment(sketch, "E1.8.2.0", {"start": v(49.54, 35.49) * mm, "end": v(59.04, 35.49) * mm});
            skLineSegment(sketch, "E1.8.2.1", {"start": v(49.54, 35.49) * mm, "end": v(49.54, 25.99) * mm});
            skLineSegment(sketch, "E1.8.2.2", {"start": v(49.54, 25.99) * mm, "end": v(59.04, 25.99) * mm});
            skLineSegment(sketch, "E1.8.2.3", {"start": v(59.04, 35.49) * mm, "end": v(59.04, 25.99) * mm});
            skLineSegment(sketch, "E1.8.3.0", {"start": v(49.54, 23.49) * mm, "end": v(59.04, 23.49) * mm});
            skLineSegment(sketch, "E1.8.3.1", {"start": v(49.54, 23.49) * mm, "end": v(49.54, 13.99) * mm});
            skLineSegment(sketch, "E1.8.3.2", {"start": v(49.54, 13.99) * mm, "end": v(59.04, 13.99) * mm});
            skLineSegment(sketch, "E1.8.3.3", {"start": v(59.04, 23.49) * mm, "end": v(59.04, 13.99) * mm});
            skLineSegment(sketch, "E1.8.4.0", {"start": v(49.54, 11.49) * mm, "end": v(59.04, 11.49) * mm});
            skLineSegment(sketch, "E1.8.4.1", {"start": v(49.54, 11.49) * mm, "end": v(49.54, 1.99) * mm});
            skLineSegment(sketch, "E1.8.4.2", {"start": v(49.54, 1.99) * mm, "end": v(59.04, 1.99) * mm});
            skLineSegment(sketch, "E1.8.4.3", {"start": v(59.04, 11.49) * mm, "end": v(59.04, 1.99) * mm});
            skLineSegment(sketch, "E1.8.5.0", {"start": v(49.54, -0.51) * mm, "end": v(59.04, -0.51) * mm});
            skLineSegment(sketch, "E1.8.5.1", {"start": v(49.54, -0.51) * mm, "end": v(49.54, -10.01) * mm});
            skLineSegment(sketch, "E1.8.5.2", {"start": v(49.54, -10.01) * mm, "end": v(59.04, -10.01) * mm});
            skLineSegment(sketch, "E1.8.5.3", {"start": v(59.04, -0.51) * mm, "end": v(59.04, -10.01) * mm});
            skLineSegment(sketch, "E1.8.6.0", {"start": v(49.54, -12.51) * mm, "end": v(59.04, -12.51) * mm});
            skLineSegment(sketch, "E1.8.6.1", {"start": v(49.54, -12.51) * mm, "end": v(49.54, -22.01) * mm});
            skLineSegment(sketch, "E1.8.6.2", {"start": v(49.54, -22.01) * mm, "end": v(59.04, -22.01) * mm});
            skLineSegment(sketch, "E1.8.6.3", {"start": v(59.04, -12.51) * mm, "end": v(59.04, -22.01) * mm});
            skLineSegment(sketch, "E1.8.7.0", {"start": v(49.54, -24.51) * mm, "end": v(59.04, -24.51) * mm});
            skLineSegment(sketch, "E1.8.7.1", {"start": v(49.54, -24.51) * mm, "end": v(49.54, -34.01) * mm});
            skLineSegment(sketch, "E1.8.7.2", {"start": v(49.54, -34.01) * mm, "end": v(59.04, -34.01) * mm});
            skLineSegment(sketch, "E1.8.7.3", {"start": v(59.04, -24.51) * mm, "end": v(59.04, -34.01) * mm});
            skLineSegment(sketch, "E1.8.8.0", {"start": v(49.54, -36.51) * mm, "end": v(59.04, -36.51) * mm});
            skLineSegment(sketch, "E1.8.8.1", {"start": v(49.54, -36.51) * mm, "end": v(49.54, -46.01) * mm});
            skLineSegment(sketch, "E1.8.8.2", {"start": v(49.54, -46.01) * mm, "end": v(59.04, -46.01) * mm});
            skLineSegment(sketch, "E1.8.8.3", {"start": v(59.04, -36.51) * mm, "end": v(59.04, -46.01) * mm});
            skLineSegment(sketch, "E1.direction1", {"start": v(-46.46, 59.49) * mm, "end": v(-34.46, 59.49) * mm, "construction": true});
            skLineSegment(sketch, "E1.direction2", {"start": v(-46.46, 59.49) * mm, "end": v(-46.46, 47.49) * mm, "construction": true});
            skSolve(sketch);
        }
        {
            var Q0;
            Q0 = qSketchRegion(id + "F0", true);
            extrude(context, id + "F1", {"entities" : qUnion([Q0]), "depth" : 160 * mm});
        }
    });
